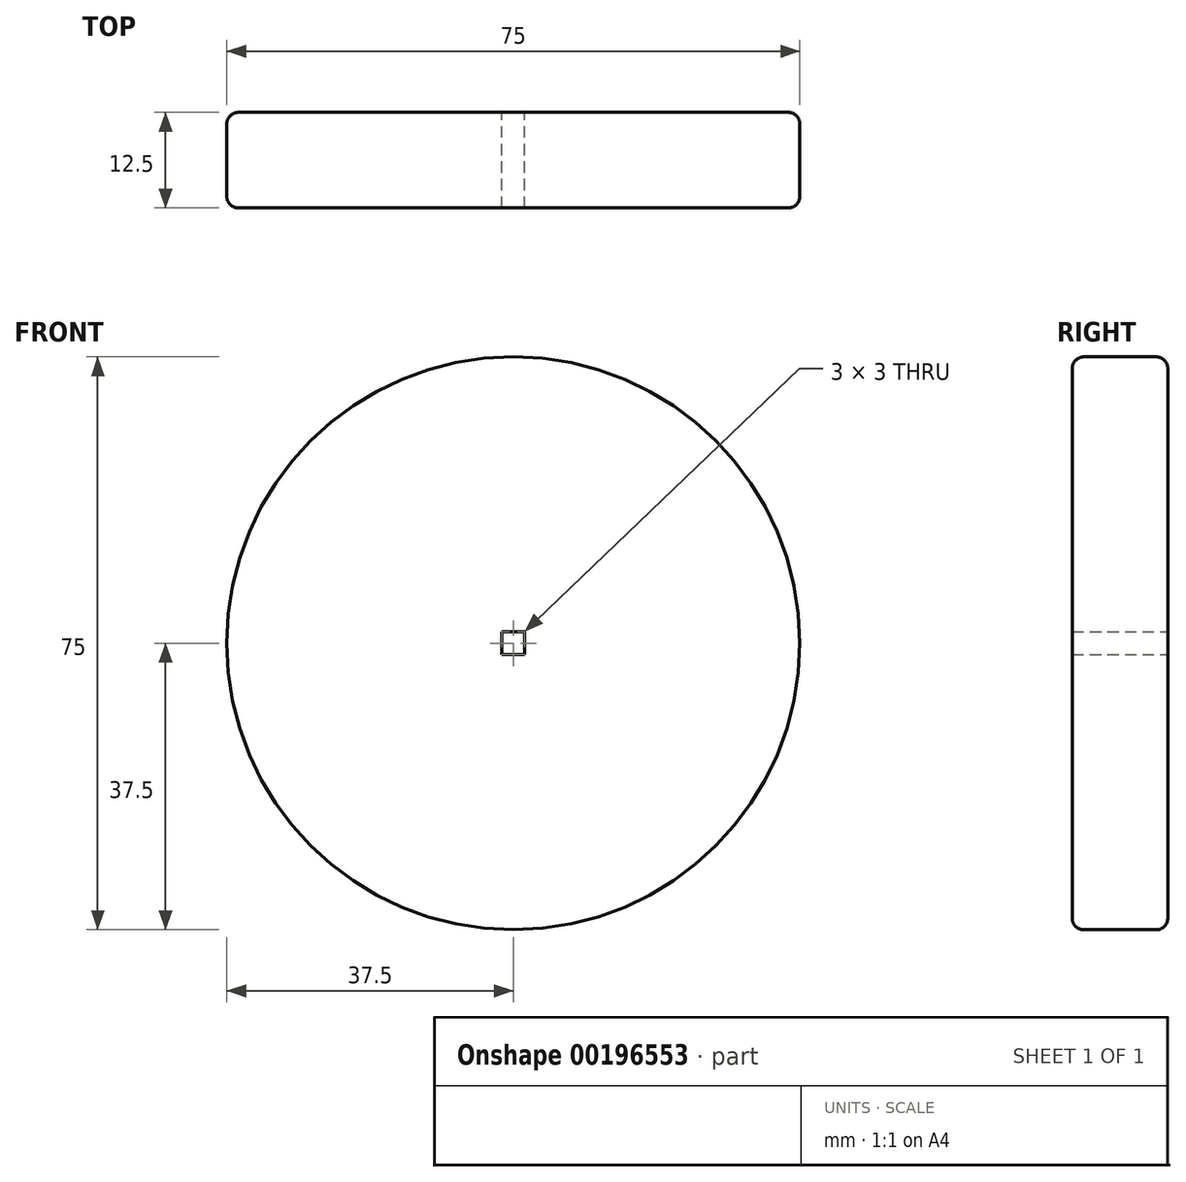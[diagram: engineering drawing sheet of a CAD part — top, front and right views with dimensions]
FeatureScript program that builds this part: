
annotation { "Feature Type Name" : "Feature", "Feature Type Description" : "" }
export const myFeature = defineFeature(function(context is Context, id is Id, definition is map)
    precondition{}
    {
        {
            var Q0;
            Q0=qCreatedBy(makeId("Front.planeOp"),FACE);
            var sketch = newSketch(context, id + "F0", { "sketchPlane" : qUnion([Q0])});
            skCircle(sketch, "E0", {"center": v(0, 0) * mm, "radius": 37.5 * mm});
            skSolve(sketch);
        }
        {
            var Q0;
            Q0 = qSketchRegion(id + "F0", true);
            extrude(context, id + "F1", {"entities" : qUnion([Q0]), "depth" : 12.5 * mm});
        }
        {
            var Q0;
            Q0=makeQuery(id+"F1.opExtrude","CAP_FACE",FACE,{"disambiguationData":[OSD([sQuery(id+"F0.wireOp",EDGE,"E0")])],"isStart":true});
            var sketch = newSketch(context, id + "F2", { "sketchPlane" : qUnion([Q0])});
            skLineSegment(sketch, "E1.bottom", {"start": v(-1.5, 1.5) * mm, "end": v(1.5, 1.5) * mm});
            skLineSegment(sketch, "E1.top", {"start": v(-1.5, -1.5) * mm, "end": v(1.5, -1.5) * mm});
            skLineSegment(sketch, "E1.left", {"start": v(-1.5, 1.5) * mm, "end": v(-1.5, -1.5) * mm});
            skLineSegment(sketch, "E1.right", {"start": v(1.5, 1.5) * mm, "end": v(1.5, -1.5) * mm});
            skSolve(sketch);
        }
        {
            var Q0;
            Q0 = qSketchRegion(id + "F2", true);
            extrude(context, id + "F3", {"entities" : qUnion([Q0]), "operationType" : NewBodyOperationType.REMOVE, "endBound" : BoundingType.UP_TO_NEXT, "oppositeDirection" : true, "depth" : 25 * mm});
        }
        {
            var Q0;
            Q0=makeQuery(id+"F1.opExtrude","CAP_EDGE",EDGE,{"disambiguationData":[OSD([sQuery(id+"F0.wireOp",EDGE,"E0")])],"isStart":true});
            var Q1;
            Q1=makeQuery(id+"F1.opExtrude","CAP_EDGE",EDGE,{"disambiguationData":[OSD([sQuery(id+"F0.wireOp",EDGE,"E0")])],"isStart":false});
            fillet(context, id + "F4", {"entities" : qUnion([Q0, Q1]), "radius" : 1.5 * mm, "tangentPropagation" : true, "allowEdgeOverflow" : false});
        }
    });
